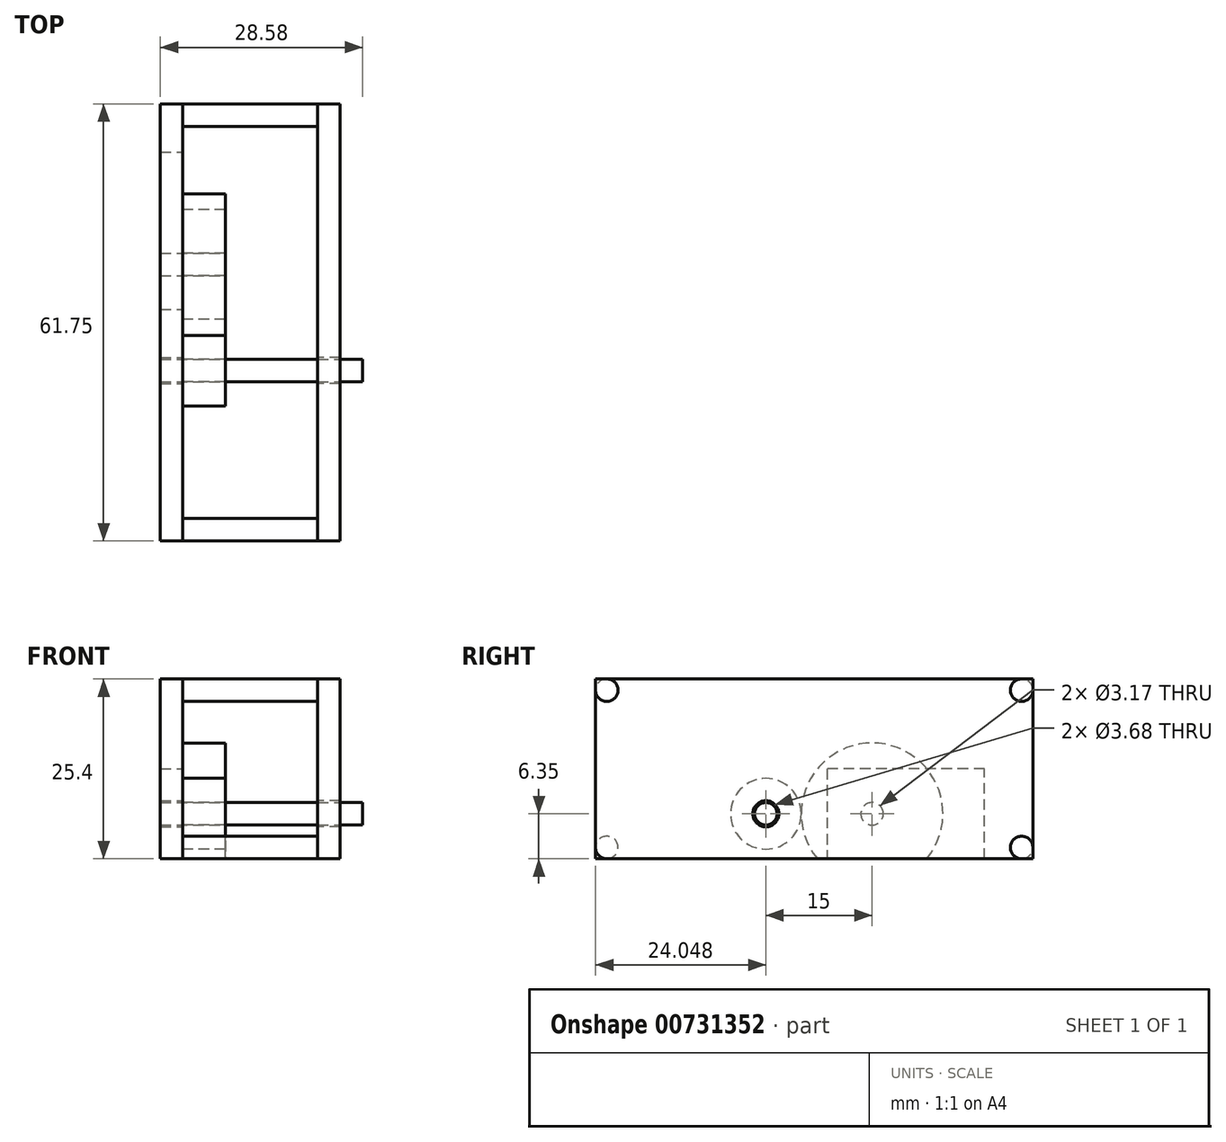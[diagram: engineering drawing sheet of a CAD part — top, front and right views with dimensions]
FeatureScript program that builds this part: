
annotation { "Feature Type Name" : "Feature", "Feature Type Description" : "" }
export const myFeature = defineFeature(function(context is Context, id is Id, definition is map)
    precondition{}
    {
        {
            var Q0;
            Q0=qCreatedBy(makeId("Right.planeOp"),FACE);
            var sketch = newSketch(context, id + "F0", { "sketchPlane" : qUnion([Q0])});
            skLineSegment(sketch, "E0", {"start": v(22.06, 6.35) * mm, "end": v(28.4, 6.35) * mm, "construction": true});
            skCircle(sketch, "E1", {"center": v(28.4, 6.35) * mm, "radius": 10 * mm});
            skLineSegment(sketch, "E2", {"start": v(28.4, 6.35) * mm, "end": v(13.4, 6.35) * mm, "construction": true});
            skCircle(sketch, "E3", {"center": v(13.4, 6.35) * mm, "radius": 5 * mm});
            skCircle(sketch, "E4", {"center": v(13.4, 6.35) * mm, "radius": 1.59 * mm});
            skCircle(sketch, "E5", {"center": v(13.4, 6.35) * mm, "radius": 1.84 * mm});
            skCircle(sketch, "E6", {"center": v(28.4, 6.35) * mm, "radius": 1.59 * mm});
            skCircle(sketch, "E7", {"center": v(28.4, 6.35) * mm, "radius": 1.84 * mm});
            skLineSegment(sketch, "E8.bottom", {"start": v(35.82, 25.4) * mm, "end": v(51.1, 25.4) * mm});
            skLineSegment(sketch, "E8.top", {"start": v(43.49, 0) * mm, "end": v(51.1, 0) * mm});
            skLineSegment(sketch, "E8.right", {"start": v(51.1, 25.4) * mm, "end": v(51.1, 0) * mm});
            skLineSegment(sketch, "E9", {"start": v(8.4, 6.35) * mm, "end": v(-10.64, 6.35) * mm, "construction": true});
            skLineSegment(sketch, "E10", {"start": v(-10.64, 0) * mm, "end": v(-10.64, 25.4) * mm});
            skCircle(sketch, "E11", {"center": v(-9.05, 23.81) * mm, "radius": 1.59 * mm});
            skPoint(sketch, "E11.first.point", {"position": v(-9.05, 25.4) * mm});
            skPoint(sketch, "E11.second.point", {"position": v(-10.64, 23.81) * mm});
            skPoint(sketch, "E11.third.point", {"position": v(-8.61, 22.29) * mm});
            skCircle(sketch, "E12", {"center": v(-9.05, 1.59) * mm, "radius": 1.59 * mm});
            skPoint(sketch, "E12.first.point", {"position": v(-10.64, 1.59) * mm});
            skPoint(sketch, "E12.second.point", {"position": v(-9.05, 0) * mm});
            skPoint(sketch, "E12.third.point", {"position": v(-8.12, 2.87) * mm});
            skCircle(sketch, "E13", {"center": v(49.52, 1.59) * mm, "radius": 1.59 * mm});
            skPoint(sketch, "E13.first.point", {"position": v(49.52, 0) * mm});
            skPoint(sketch, "E13.second.point", {"position": v(51.1, 1.59) * mm});
            skPoint(sketch, "E13.third.point", {"position": v(47.96, 1.9) * mm});
            skCircle(sketch, "E14", {"center": v(49.52, 23.81) * mm, "radius": 1.59 * mm});
            skPoint(sketch, "E14.first.point", {"position": v(49.52, 25.4) * mm});
            skPoint(sketch, "E14.second.point", {"position": v(51.1, 23.81) * mm});
            skPoint(sketch, "E14.third.point", {"position": v(47.97, 23.48) * mm});
            skLineSegment(sketch, "E15.bottom", {"start": v(35.82, 25.4) * mm, "end": v(41.82, 25.4) * mm});
            skLineSegment(sketch, "E15.top", {"start": v(44.28, 0) * mm, "end": v(50.28, 0) * mm});
            skLineSegment(sketch, "E16", {"start": v(-10.64, 25.4) * mm, "end": v(35.82, 25.4) * mm});
            skLineSegment(sketch, "E17", {"start": v(44.28, 0) * mm, "end": v(44.28, 12.7) * mm});
            skLineSegment(sketch, "E18", {"start": v(44.28, 12.7) * mm, "end": v(22.06, 12.7) * mm});
            skPoint(sketch, "E18.endSnap0", {"position": v(22.06, 3.17) * mm});
            skLineSegment(sketch, "E19", {"start": v(22.06, 12.7) * mm, "end": v(22.06, 0) * mm});
            skLineSegment(sketch, "E20", {"start": v(-10.64, 0) * mm, "end": v(51.1, 0) * mm});
            skSolve(sketch);
        }
        {
            var Q0;
            {var subQ7=sQuery(id+"F0.wireOp",EDGE,"E3");Q0=makeQuery(id+"F0.imprint","IMPRINT",FACE,{"disambiguationData":[TD([[makeQuery(id+"F0.imprint","IMPRINT",EDGE,{"derivedFrom":subQ7}),-1.0]])]});}
            var Q1;
            {var subQ0=sQuery(id+"F0.wireOp",EDGE,"E8.right");var subQ1=sQuery(id+"F0.wireOp",EDGE,"E8.bottom");var subQ2=makeQuery(id+"F0.imprint","INTERSECT",VERTEX,{"derivedFrom":[subQ1,subQ0]});Q1=makeQuery(id+"F0.imprint","IMPRINT",FACE,{"disambiguationData":[TD([[makeQuery(id+"F0.imprint","IMPRINT",EDGE,{"disambiguationData":[TD([[subQ2,1.0]])],"derivedFrom":subQ1}),-1.0]])]});}
            var Q2;
            {var subQ0=sQuery(id+"F0.wireOp",EDGE,"E8.right");var subQ1=sQuery(id+"F0.wireOp",EDGE,"E8.top");var subQ2=makeQuery(id+"F0.imprint","INTERSECT",VERTEX,{"derivedFrom":[subQ1,subQ0]});Q2=makeQuery(id+"F0.imprint","IMPRINT",FACE,{"disambiguationData":[TD([[makeQuery(id+"F0.imprint","IMPRINT",EDGE,{"disambiguationData":[TD([[subQ2,1.0]])],"derivedFrom":subQ1}),1.0]])]});}
            var Q3;
            {var subQ0=sQuery(id+"F0.wireOp",EDGE,"E10");var subQ1=sQuery(id+"F0.wireOp",EDGE,"mzH20aDh-REpL-ww0y-ika9-ryDnuCNVRDq3");var subQ2=makeQuery(id+"F0.imprint","INTERSECT",VERTEX,{"derivedFrom":[subQ1,subQ0]});Q3=makeQuery(id+"F0.imprint","IMPRINT",FACE,{"disambiguationData":[TD([[makeQuery(id+"F0.imprint","IMPRINT",EDGE,{"disambiguationData":[TD([[subQ2,1.0]])],"derivedFrom":subQ1}),1.0]])]});}
            var Q4;
            {var subQ0=sQuery(id+"F0.wireOp",EDGE,"E10");var subQ1=sQuery(id+"F0.wireOp",EDGE,"AjtEDcku-NLsd-kfh1-AKqZ-MW7YpeOLVoxd");var subQ2=makeQuery(id+"F0.imprint","INTERSECT",VERTEX,{"derivedFrom":[subQ1,subQ0]});Q4=makeQuery(id+"F0.imprint","IMPRINT",FACE,{"disambiguationData":[TD([[makeQuery(id+"F0.imprint","IMPRINT",EDGE,{"disambiguationData":[TD([[subQ2,-1.0]])],"derivedFrom":subQ1}),1.0]])]});}
            var Q5;
            Q5=makeQuery(id+"F0.imprint","IMPRINT",FACE,{"disambiguationData":[TD([[makeQuery(id+"F0.imprint","IMPRINT",EDGE,{"derivedFrom":sQuery(id+"F0.wireOp",EDGE,"E3")}),1.0]])]});
            var Q6;
            {var subQ0=sQuery(id+"F0.wireOp",EDGE,"E14");var subQ1=makeQuery(id+"F0.imprint","INTERSECT",VERTEX,{"derivedFrom":[sQuery(id+"F0.wireOp",EDGE,"E8.bottom"),subQ0]});Q6=makeQuery(id+"F0.imprint","IMPRINT",FACE,{"disambiguationData":[TD([[makeQuery(id+"F0.imprint","IMPRINT",EDGE,{"disambiguationData":[TD([[subQ1,1.0]])],"derivedFrom":subQ0}),1.0]])]});}
            var Q7;
            {var subQ0=sQuery(id+"F0.wireOp",EDGE,"E13");var subQ1=makeQuery(id+"F0.imprint","INTERSECT",VERTEX,{"derivedFrom":[sQuery(id+"F0.wireOp",EDGE,"E8.top"),subQ0]});Q7=makeQuery(id+"F0.imprint","IMPRINT",FACE,{"disambiguationData":[TD([[makeQuery(id+"F0.imprint","IMPRINT",EDGE,{"disambiguationData":[TD([[subQ1,1.0]])],"derivedFrom":subQ0}),1.0]])]});}
            var Q8;
            {var subQ0=sQuery(id+"F0.wireOp",EDGE,"E12");var subQ1=makeQuery(id+"F0.imprint","INTERSECT",VERTEX,{"derivedFrom":[sQuery(id+"F0.wireOp",EDGE,"AjtEDcku-NLsd-kfh1-AKqZ-MW7YpeOLVoxd"),subQ0]});Q8=makeQuery(id+"F0.imprint","IMPRINT",FACE,{"disambiguationData":[TD([[makeQuery(id+"F0.imprint","IMPRINT",EDGE,{"disambiguationData":[TD([[subQ1,1.0]])],"derivedFrom":subQ0}),1.0]])]});}
            var Q9;
            {var subQ0=sQuery(id+"F0.wireOp",EDGE,"E11");var subQ1=makeQuery(id+"F0.imprint","INTERSECT",VERTEX,{"derivedFrom":[sQuery(id+"F0.wireOp",EDGE,"mzH20aDh-REpL-ww0y-ika9-ryDnuCNVRDq3"),subQ0]});Q9=makeQuery(id+"F0.imprint","IMPRINT",FACE,{"disambiguationData":[TD([[makeQuery(id+"F0.imprint","IMPRINT",EDGE,{"disambiguationData":[TD([[subQ1,-1.0]])],"derivedFrom":subQ0}),1.0]])]});}
            var Q10;
            {var subQ0=sQuery(id+"F0.wireOp",EDGE,"E14");var subQ1=sQuery(id+"F0.wireOp",EDGE,"E8.right");var subQ2=makeQuery(id+"F0.imprint","INTERSECT",VERTEX,{"derivedFrom":[subQ1,subQ0]});Q10=makeQuery(id+"F0.imprint","IMPRINT",FACE,{"disambiguationData":[TD([[makeQuery(id+"F0.imprint","IMPRINT",EDGE,{"disambiguationData":[TD([[subQ2,-1.0]])],"derivedFrom":subQ1}),-1.0]])]});}
            var Q11;
            {var subQ0=sQuery(id+"F0.wireOp",EDGE,"E15.top");var subQ1=sQuery(id+"F0.wireOp",EDGE,"E13");var subQ2=makeQuery(id+"F0.imprint","INTERSECT",VERTEX,{"derivedFrom":[subQ1,subQ0]});Q11=makeQuery(id+"F0.imprint","IMPRINT",FACE,{"disambiguationData":[TD([[makeQuery(id+"F0.imprint","IMPRINT",EDGE,{"disambiguationData":[TD([[subQ2,1.0]])],"derivedFrom":subQ1}),-1.0]])]});}
            var Q12;
            {var subQ0=sQuery(id+"F0.wireOp",EDGE,"E15.top");var subQ1=sQuery(id+"F0.wireOp",EDGE,"E8.right");var subQ2=makeQuery(id+"F0.imprint","INTERSECT",VERTEX,{"derivedFrom":[subQ1,subQ0]});Q12=makeQuery(id+"F0.imprint","IMPRINT",FACE,{"disambiguationData":[TD([[makeQuery(id+"F0.imprint","IMPRINT",EDGE,{"disambiguationData":[TD([[subQ2,1.0]])],"derivedFrom":subQ1}),-1.0]])]});}
            var Q13;
            {var subQ0=sQuery(id+"F0.wireOp",EDGE,"E15.bottom");var subQ1=sQuery(id+"F0.wireOp",EDGE,"E14");var subQ2=makeQuery(id+"F0.imprint","INTERSECT",VERTEX,{"derivedFrom":[subQ1,subQ0]});Q13=makeQuery(id+"F0.imprint","IMPRINT",FACE,{"disambiguationData":[TD([[makeQuery(id+"F0.imprint","IMPRINT",EDGE,{"disambiguationData":[TD([[subQ2,-1.0]])],"derivedFrom":subQ1}),-1.0]])]});}
            var Q14;
            {var subQ0=sQuery(id+"F0.wireOp",EDGE,"E15.bottom");var subQ1=sQuery(id+"F0.wireOp",EDGE,"E8.right");var subQ2=makeQuery(id+"F0.imprint","INTERSECT",VERTEX,{"derivedFrom":[subQ1,subQ0]});Q14=makeQuery(id+"F0.imprint","IMPRINT",FACE,{"disambiguationData":[TD([[makeQuery(id+"F0.imprint","IMPRINT",EDGE,{"disambiguationData":[TD([[subQ2,-1.0]])],"derivedFrom":subQ1}),-1.0]])]});}
            var Q15;
            {var subQ0=sQuery(id+"F0.wireOp",EDGE,"E16");var subQ1=sQuery(id+"F0.wireOp",EDGE,"E10");var subQ2=makeQuery(id+"F0.imprint","INTERSECT",VERTEX,{"derivedFrom":[subQ1,subQ0]});Q15=makeQuery(id+"F0.imprint","IMPRINT",FACE,{"disambiguationData":[TD([[makeQuery(id+"F0.imprint","IMPRINT",EDGE,{"disambiguationData":[TD([[subQ2,1.0]])],"derivedFrom":subQ1}),-1.0]])]});}
            var Q16;
            {var subQ0=sQuery(id+"F0.wireOp",EDGE,"E19");Q16=makeQuery(id+"F0.imprint","IMPRINT",FACE,{"disambiguationData":[TD([[makeQuery(id+"F0.imprint","IMPRINT",EDGE,{"derivedFrom":subQ0}),-1.0]])]});}
            var Q17;
            {var subQ0=sQuery(id+"F0.wireOp",EDGE,"E17");Q17=makeQuery(id+"F0.imprint","IMPRINT",FACE,{"disambiguationData":[TD([[makeQuery(id+"F0.imprint","IMPRINT",EDGE,{"derivedFrom":subQ0}),1.0]])]});}
            var Q18;
            Q18=makeQuery(id+"F0.imprint","IMPRINT",FACE,{"disambiguationData":[TD([[makeQuery(id+"F0.imprint","IMPRINT",EDGE,{"derivedFrom":sQuery(id+"F0.wireOp",EDGE,"E7")}),-1.0]])]});
            var Q19;
            Q19=makeQuery(id+"F0.imprint","IMPRINT",FACE,{"disambiguationData":[TD([[makeQuery(id+"F0.imprint","IMPRINT",EDGE,{"derivedFrom":sQuery(id+"F0.wireOp",EDGE,"E6")}),1.0]])]});
            var Q20;
            Q20=makeQuery(id+"F0.imprint","IMPRINT",FACE,{"disambiguationData":[TD([[makeQuery(id+"F0.imprint","IMPRINT",EDGE,{"derivedFrom":sQuery(id+"F0.wireOp",EDGE,"E6")}),-1.0]])]});
            extrude(context, id + "F1", {"entities" : qUnion([Q0, Q1, Q2, Q3, Q4, Q5, Q6, Q7, Q8, Q9, Q10, Q11, Q12, Q13, Q14, Q15, Q16, Q17, Q18, Q19, Q20]), "depth" : 3.17 * mm, "offsetDistance" : 25.4 * mm});
        }
        {
            var Q0;
            {var subQ0=sQuery(id+"F0.wireOp",EDGE,"E14");var subQ1=makeQuery(id+"F0.imprint","INTERSECT",VERTEX,{"derivedFrom":[sQuery(id+"F0.wireOp",EDGE,"E8.bottom"),subQ0]});Q0=makeQuery(id+"F0.imprint","IMPRINT",FACE,{"disambiguationData":[TD([[makeQuery(id+"F0.imprint","IMPRINT",EDGE,{"disambiguationData":[TD([[subQ1,1.0]])],"derivedFrom":subQ0}),1.0]])]});}
            var Q1;
            {var subQ0=sQuery(id+"F0.wireOp",EDGE,"E13");var subQ1=makeQuery(id+"F0.imprint","INTERSECT",VERTEX,{"derivedFrom":[sQuery(id+"F0.wireOp",EDGE,"E8.top"),subQ0]});Q1=makeQuery(id+"F0.imprint","IMPRINT",FACE,{"disambiguationData":[TD([[makeQuery(id+"F0.imprint","IMPRINT",EDGE,{"disambiguationData":[TD([[subQ1,1.0]])],"derivedFrom":subQ0}),1.0]])]});}
            var Q2;
            {var subQ0=sQuery(id+"F0.wireOp",EDGE,"E12");var subQ1=makeQuery(id+"F0.imprint","INTERSECT",VERTEX,{"derivedFrom":[sQuery(id+"F0.wireOp",EDGE,"AjtEDcku-NLsd-kfh1-AKqZ-MW7YpeOLVoxd"),subQ0]});Q2=makeQuery(id+"F0.imprint","IMPRINT",FACE,{"disambiguationData":[TD([[makeQuery(id+"F0.imprint","IMPRINT",EDGE,{"disambiguationData":[TD([[subQ1,1.0]])],"derivedFrom":subQ0}),1.0]])]});}
            var Q3;
            {var subQ0=sQuery(id+"F0.wireOp",EDGE,"E11");var subQ1=makeQuery(id+"F0.imprint","INTERSECT",VERTEX,{"derivedFrom":[sQuery(id+"F0.wireOp",EDGE,"mzH20aDh-REpL-ww0y-ika9-ryDnuCNVRDq3"),subQ0]});Q3=makeQuery(id+"F0.imprint","IMPRINT",FACE,{"disambiguationData":[TD([[makeQuery(id+"F0.imprint","IMPRINT",EDGE,{"disambiguationData":[TD([[subQ1,-1.0]])],"derivedFrom":subQ0}),1.0]])]});}
            extrude(context, id + "F2", {"entities" : qUnion([Q0, Q1, Q2, Q3]), "oppositeDirection" : true, "depth" : 19.05 * mm, "offsetDistance" : 25.4 * mm});
        }
        {
            var Q0;
            Q0=makeQuery(id+"F2.opExtrude","CAP_FACE",FACE,{"disambiguationData":[OSD([sQuery(id+"F0.wireOp",EDGE,"E14")])],"isStart":false});
            var sketch = newSketch(context, id + "F3", { "sketchPlane" : qUnion([Q0])});
            skLineSegment(sketch, "E21.bottom", {"start": v(-51.1, 25.4) * mm, "end": v(10.64, 25.4) * mm});
            skLineSegment(sketch, "E21.top", {"start": v(-51.1, 0) * mm, "end": v(10.64, 0) * mm});
            skLineSegment(sketch, "E21.left", {"start": v(-51.1, 25.4) * mm, "end": v(-51.1, 0) * mm});
            skLineSegment(sketch, "E21.right", {"start": v(10.64, 25.4) * mm, "end": v(10.64, 0) * mm});
            skLineSegment(sketch, "E22", {"start": v(-44.28, 6.35) * mm, "end": v(-44.28, 0) * mm, "construction": true});
            skLineSegment(sketch, "E23", {"start": v(-44.28, 6.35) * mm, "end": v(-22.06, 6.35) * mm, "construction": true});
            skLineSegment(sketch, "E24", {"start": v(-22.06, 6.35) * mm, "end": v(-22.06, 0) * mm, "construction": true});
            skLineSegment(sketch, "E25", {"start": v(-22.06, 6.35) * mm, "end": v(-28.4, 6.35) * mm});
            skCircle(sketch, "E26", {"center": v(-28.4, 6.35) * mm, "radius": 10 * mm});
            skLineSegment(sketch, "E27", {"start": v(-28.4, 6.35) * mm, "end": v(-13.4, 6.35) * mm, "construction": true});
            skCircle(sketch, "E28", {"center": v(-13.4, 6.35) * mm, "radius": 5 * mm});
            skCircle(sketch, "E29", {"center": v(-13.4, 6.35) * mm, "radius": 1.59 * mm});
            skCircle(sketch, "E30", {"center": v(-13.4, 6.35) * mm, "radius": 1.84 * mm});
            skCircle(sketch, "E31", {"center": v(-28.4, 6.35) * mm, "radius": 1.84 * mm});
            skCircle(sketch, "E32", {"center": v(-28.4, 6.35) * mm, "radius": 1.59 * mm});
            skLineSegment(sketch, "E33", {"start": v(-44.28, 0) * mm, "end": v(-44.28, 12.7) * mm});
            skLineSegment(sketch, "E34", {"start": v(-44.28, 12.7) * mm, "end": v(-22.06, 12.7) * mm});
            skLineSegment(sketch, "E35", {"start": v(-22.06, 12.7) * mm, "end": v(-22.06, 0) * mm});
            skSolve(sketch);
        }
        {
            var Q0;
            {var subQ0=sQuery(id+"F3.wireOp",EDGE,"61rDZBB9-DkLB-R1jF-Ugw1-9J4s0qTPQNlm");var subQ1=sQuery(id+"F3.wireOp",EDGE,"E21.top");var subQ2=makeQuery(id+"F3.imprint","INTERSECT",VERTEX,{"disambiguationData":[OD(0.0)],"derivedFrom":[subQ1,subQ0]});Q0=makeQuery(id+"F3.imprint","IMPRINT",FACE,{"disambiguationData":[TD([[makeQuery(id+"F3.imprint","IMPRINT",EDGE,{"disambiguationData":[TD([[subQ2,-1.0]])],"derivedFrom":subQ1}),1.0]])]});}
            var Q1;
            Q1=makeQuery(id+"F3.imprint","IMPRINT",FACE,{"disambiguationData":[TD([[makeQuery(id+"F3.imprint","IMPRINT",EDGE,{"derivedFrom":sQuery(id+"F3.wireOp",EDGE,"f6RzX2im-ddRW-lgic-JvNA-CsLhbOmZ7d9f")}),1.0]])]});
            var Q2;
            {var subQ0=sQuery(id+"F3.wireOp",EDGE,"E21.right");Q2=makeQuery(id+"F3.imprint","IMPRINT",FACE,{"disambiguationData":[TD([[makeQuery(id+"F3.imprint","IMPRINT",EDGE,{"derivedFrom":subQ0}),-1.0]])]});}
            var Q3;
            {var subQ0=sQuery(id+"F3.wireOp",EDGE,"E21.left");var subQ1=sQuery(id+"F3.wireOp",EDGE,"E21.bottom");var subQ2=makeQuery(id+"F3.imprint","INTERSECT",VERTEX,{"derivedFrom":[subQ1,subQ0]});Q3=makeQuery(id+"F3.imprint","IMPRINT",FACE,{"disambiguationData":[TD([[makeQuery(id+"F3.imprint","IMPRINT",EDGE,{"disambiguationData":[TD([[subQ2,-1.0]])],"derivedFrom":subQ1}),-1.0]])]});}
            var Q4;
            {var subQ0=makeQuery(id+"F2.opExtrude","CAP_EDGE",EDGE,{"disambiguationData":[OSD([sQuery(id+"F0.wireOp",EDGE,"E14")])],"isStart":false});var subQ1=makeQuery(id+"F3.imprint","INTERSECT",VERTEX,{"derivedFrom":[subQ0,sQuery(id+"F3.wireOp",EDGE,"E21.bottom")]});Q4=makeQuery(id+"F3.imprint","IMPRINT",FACE,{"disambiguationData":[TD([[makeQuery(id+"F3.imprint","IMPRINT",EDGE,{"disambiguationData":[TD([[subQ1,1.0]])],"derivedFrom":subQ0}),-1.0]])]});}
            var Q5;
            Q5=makeQuery(id+"F3.imprint","IMPRINT",FACE,{"disambiguationData":[TD([[makeQuery(id+"F3.imprint","IMPRINT",EDGE,{"derivedFrom":sQuery(id+"F3.wireOp",EDGE,"E28")}),1.0]])]});
            var Q6;
            {var subQ0=sQuery(id+"F3.wireOp",EDGE,"E35");var subQ9=makeQuery(id+"F3.imprint","IMPRINT",VERTEX,{"derivedFrom":subQ0});Q6=makeQuery(id+"F3.imprint","IMPRINT",FACE,{"disambiguationData":[TD([[makeQuery(id+"F3.imprint","IMPRINT",EDGE,{"disambiguationData":[TD([[subQ9,1.0]])],"derivedFrom":subQ0}),1.0]])]});}
            extrude(context, id + "F4", {"entities" : qUnion([Q0, Q1, Q2, Q3, Q4, Q5, Q6]), "operationType" : NewBodyOperationType.ADD, "depth" : 3.17 * mm, "offsetDistance" : 25.4 * mm});
        }
        {
            var Q0;
            Q0=makeQuery(id+"F3.imprint","IMPRINT",FACE,{"disambiguationData":[TD([[makeQuery(id+"F3.imprint","IMPRINT",EDGE,{"derivedFrom":sQuery(id+"F3.wireOp",EDGE,"E32")}),1.0]])]});
            extrude(context, id + "F5", {"entities" : qUnion([Q0]), "depth" : 3.17 * mm, "offsetDistance" : 25.4 * mm});
        }
        {
            var Q0;
            Q0=makeQuery(id+"F3.imprint","IMPRINT",FACE,{"disambiguationData":[TD([[makeQuery(id+"F3.imprint","IMPRINT",EDGE,{"derivedFrom":sQuery(id+"F3.wireOp",EDGE,"E32")}),1.0]])]});
            extrude(context, id + "F6", {"entities" : qUnion([Q0]), "operationType" : NewBodyOperationType.ADD, "oppositeDirection" : true, "depth" : 6 * mm, "offsetDistance" : 25.4 * mm});
        }
        {
            var Q0;
            {var subQ0=sQuery(id+"F3.wireOp",EDGE,"E26");var subQ1=sQuery(id+"F3.wireOp",EDGE,"E21.top");var subQ2=makeQuery(id+"F3.imprint","INTERSECT",VERTEX,{"disambiguationData":[OD(0.0)],"derivedFrom":[subQ1,subQ0]});Q0=makeQuery(id+"F3.imprint","IMPRINT",FACE,{"disambiguationData":[TD([[makeQuery(id+"F3.imprint","IMPRINT",EDGE,{"disambiguationData":[TD([[subQ2,-1.0]])],"derivedFrom":subQ1}),-1.0]])]});}
            var Q1;
            Q1=makeQuery(id+"F3.imprint","IMPRINT",FACE,{"disambiguationData":[TD([[makeQuery(id+"F3.imprint","IMPRINT",EDGE,{"derivedFrom":sQuery(id+"F3.wireOp",EDGE,"E31")}),-1.0]])]});
            var Q2;
            Q2=makeQuery(id+"F3.imprint","IMPRINT",FACE,{"disambiguationData":[TD([[makeQuery(id+"F3.imprint","IMPRINT",EDGE,{"derivedFrom":sQuery(id+"F3.wireOp",EDGE,"E31")}),1.0]])]});
            var Q3;
            {var subQ0=sQuery(id+"F3.wireOp",EDGE,"E35");var subQ9=makeQuery(id+"F3.imprint","IMPRINT",VERTEX,{"derivedFrom":subQ0});Q3=makeQuery(id+"F3.imprint","IMPRINT",FACE,{"disambiguationData":[TD([[makeQuery(id+"F3.imprint","IMPRINT",EDGE,{"disambiguationData":[TD([[subQ9,1.0]])],"derivedFrom":subQ0}),1.0]])]});}
            extrude(context, id + "F7", {"entities" : qUnion([Q0, Q1, Q2, Q3]), "oppositeDirection" : true, "depth" : 6 * mm, "offsetDistance" : 25.4 * mm});
        }
        {
            var Q0;
            Q0=makeQuery(id+"F3.imprint","IMPRINT",FACE,{"disambiguationData":[TD([[makeQuery(id+"F3.imprint","IMPRINT",EDGE,{"derivedFrom":sQuery(id+"F3.wireOp",EDGE,"E29")}),1.0]])]});
            extrude(context, id + "F8", {"entities" : qUnion([Q0]), "depth" : 3.17 * mm, "offsetDistance" : 25.4 * mm});
        }
        {
            var Q0;
            Q0=makeQuery(id+"F3.imprint","IMPRINT",FACE,{"disambiguationData":[TD([[makeQuery(id+"F3.imprint","IMPRINT",EDGE,{"derivedFrom":sQuery(id+"F3.wireOp",EDGE,"E29")}),1.0]])]});
            extrude(context, id + "F9", {"entities" : qUnion([Q0]), "operationType" : NewBodyOperationType.ADD, "oppositeDirection" : true, "depth" : 25.4 * mm, "offsetDistance" : 25.4 * mm});
        }
        {
            var Q0;
            Q0=makeQuery(id+"F3.imprint","IMPRINT",FACE,{"disambiguationData":[TD([[makeQuery(id+"F3.imprint","IMPRINT",EDGE,{"derivedFrom":sQuery(id+"F3.wireOp",EDGE,"E28")}),1.0]])]});
            var Q1;
            Q1=makeQuery(id+"F3.imprint","IMPRINT",FACE,{"disambiguationData":[TD([[makeQuery(id+"F3.imprint","IMPRINT",EDGE,{"derivedFrom":sQuery(id+"F3.wireOp",EDGE,"E29")}),-1.0]])]});
            extrude(context, id + "F10", {"entities" : qUnion([Q0, Q1]), "oppositeDirection" : true, "depth" : 6 * mm, "offsetDistance" : 25.4 * mm});
        }
    });
